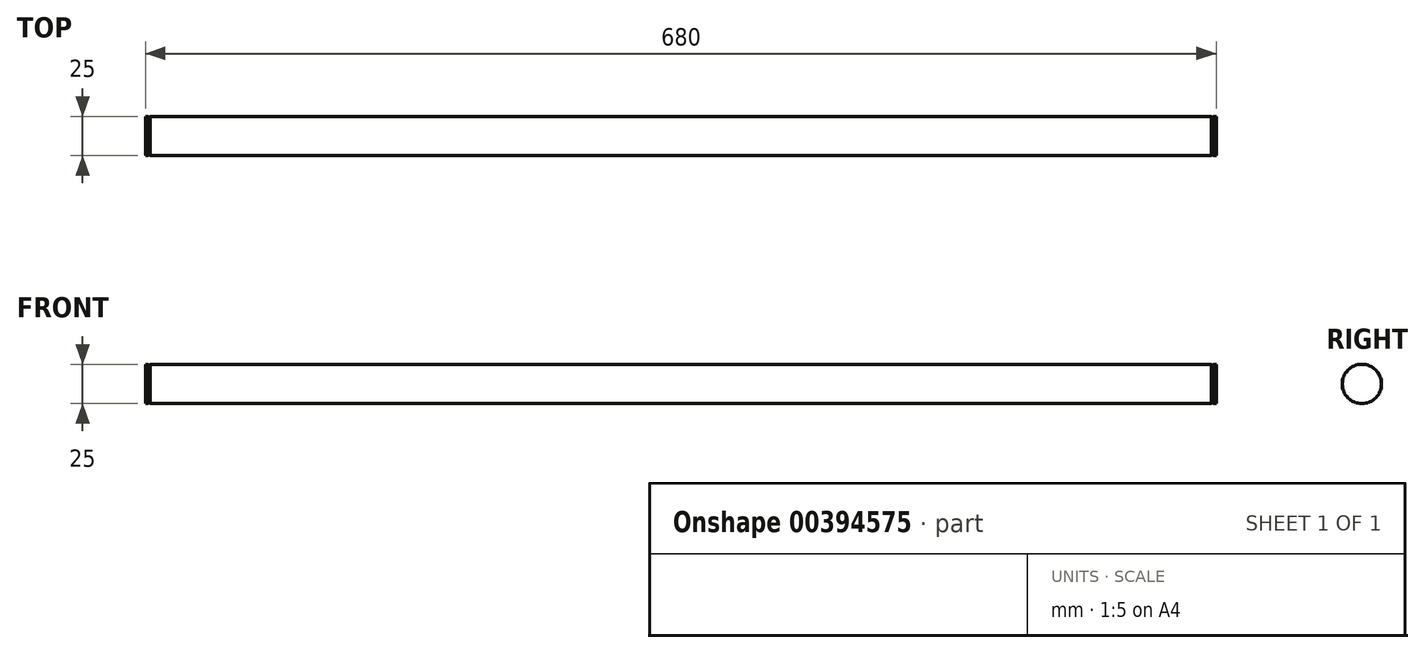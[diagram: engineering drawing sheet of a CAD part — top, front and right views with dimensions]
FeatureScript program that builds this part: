
annotation { "Feature Type Name" : "Feature", "Feature Type Description" : "" }
export const myFeature = defineFeature(function(context is Context, id is Id, definition is map)
    precondition{}
    {
        {
            var Q0;
            Q0=qCreatedBy(makeId("Right.planeOp"),FACE);
            var sketch = newSketch(context, id + "F0", { "sketchPlane" : qUnion([Q0])});
            skCircle(sketch, "E0", {"center": v(0, 0) * mm, "radius": 12.5 * mm});
            skSolve(sketch);
        }
        {
            var Q0;
            Q0 = qSketchRegion(id + "F0", true);
            extrude(context, id + "F1", {"entities" : qUnion([Q0]), "endBound" : BoundingType.SYMMETRIC, "depth" : 674 * mm});
        }
        {
            var Q0;
            Q0=makeQuery(id+"F1.opExtrude","CAP_FACE",FACE,{"disambiguationData":[OSD([sQuery(id+"F0.wireOp",EDGE,"E0")])],"isStart":false});
            var sketch = newSketch(context, id + "F2", { "sketchPlane" : qUnion([Q0])});
            skCircle(sketch, "E1", {"center": v(0, 0) * mm, "radius": 11.95 * mm});
            skSolve(sketch);
        }
        {
            var Q0;
            Q0 = qSketchRegion(id + "F2", true);
            extrude(context, id + "F3", {"entities" : qUnion([Q0]), "operationType" : NewBodyOperationType.ADD, "depth" : 1.3 * mm});
        }
        {
            var Q0;
            Q0=makeQuery(id+"F3.opExtrude","CAP_FACE",FACE,{"disambiguationData":[OSD([sQuery(id+"F2.wireOp",EDGE,"E1")])],"isStart":false});
            var sketch = newSketch(context, id + "F4", { "sketchPlane" : qUnion([Q0])});
            skCircle(sketch, "E2", {"center": v(0, 0) * mm, "radius": 12.5 * mm});
            skSolve(sketch);
        }
        {
            var Q0;
            Q0 = qSketchRegion(id + "F4", true);
            extrude(context, id + "F5", {"entities" : qUnion([Q0]), "operationType" : NewBodyOperationType.ADD, "depth" : 1.7 * mm});
        }
        {
            var Q0;
            Q0=makeQuery(id+"F1.opExtrude","SWEPT_BODY",BODY,{"disambiguationData":[OSD([sQuery(id+"F0.wireOp",EDGE,"E0")])]});
            var Q1;
            Q1=qCreatedBy(makeId("Right.planeOp"),FACE);
            mirror(context, id + "F6", {"operationType" : NewBodyOperationType.ADD, "entities" : qUnion([Q0]), "mirrorPlane" : qUnion([Q1])});
        }
    });
